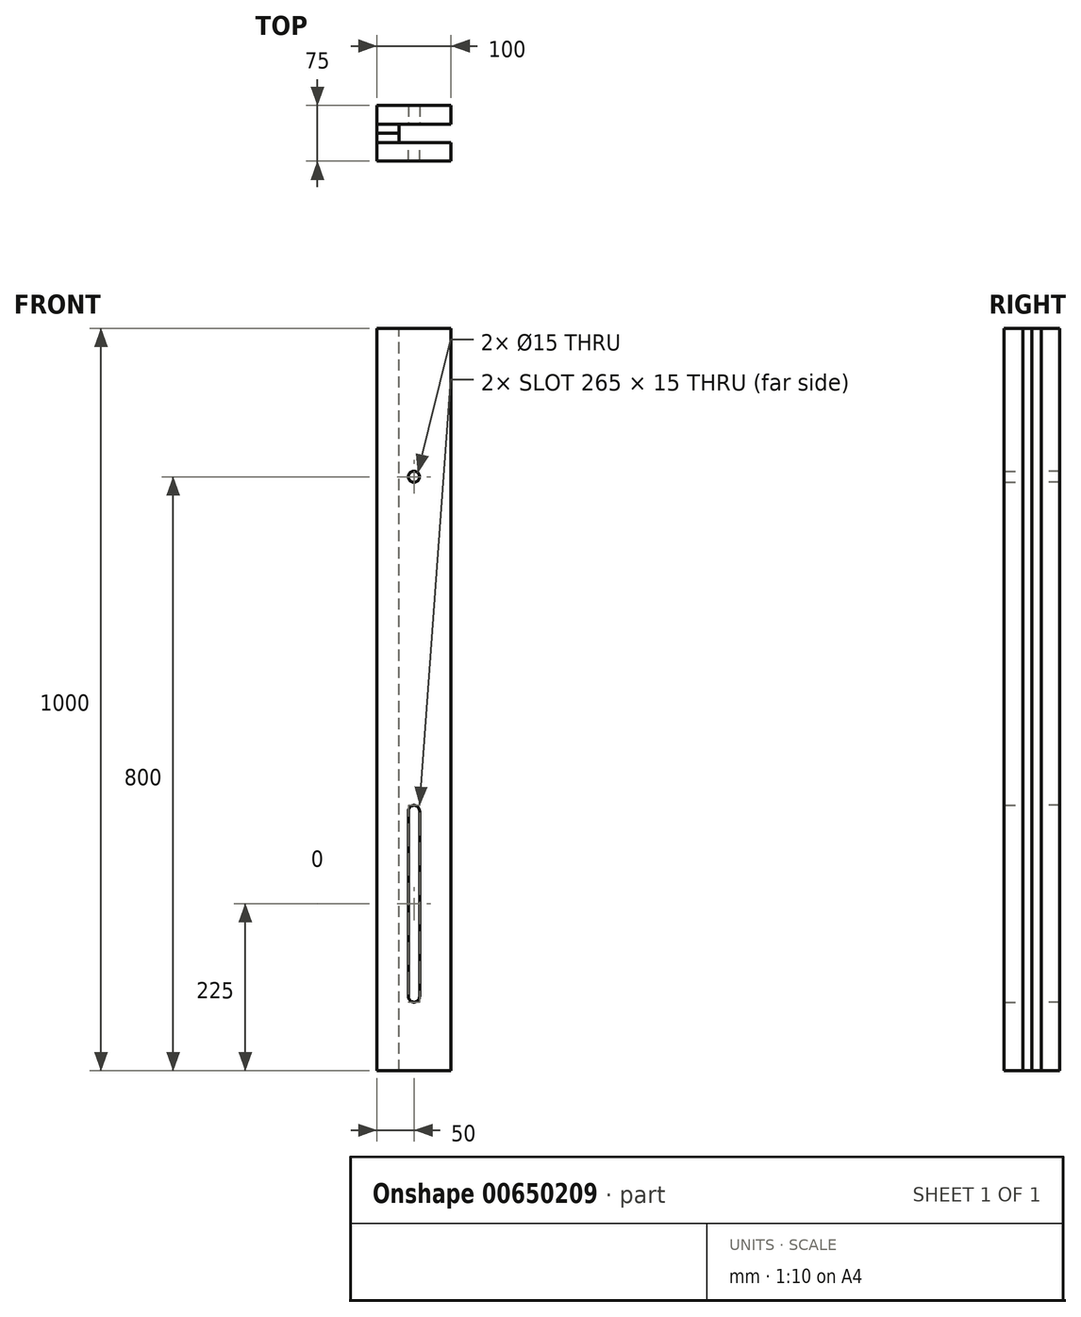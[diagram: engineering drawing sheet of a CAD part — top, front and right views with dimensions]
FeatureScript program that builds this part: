
annotation { "Feature Type Name" : "Feature", "Feature Type Description" : "" }
export const myFeature = defineFeature(function(context is Context, id is Id, definition is map)
    precondition{}
    {
        {
            var Q0;
            Q0=qCreatedBy(makeId("Front.planeOp"),FACE);
            var sketch = newSketch(context, id + "F0", { "sketchPlane" : qUnion([Q0])});
            skLineSegment(sketch, "E0.bottom", {"start": v(0, 0) * mm, "end": v(100, 0) * mm});
            skLineSegment(sketch, "E0.top", {"start": v(0, 1000) * mm, "end": v(100, 1000) * mm});
            skLineSegment(sketch, "E0.left", {"start": v(0, 0) * mm, "end": v(0, 1000) * mm});
            skLineSegment(sketch, "E0.right", {"start": v(100, 0) * mm, "end": v(100, 1000) * mm});
            skLineSegment(sketch, "E1", {"start": v(50, 100) * mm, "end": v(50, 350) * mm});
            skPoint(sketch, "E1.startSnap0", {"position": v(50, 0) * mm});
            skArc(sketch, "E2.0.startCap", {"start": v(57.5, 100) * mm, "mid": v(50, 92.5) * mm, "end": v(42.5, 100) * mm});
            skArc(sketch, "E2.0.endCap", {"start": v(42.5, 350) * mm, "mid": v(50, 357.5) * mm, "end": v(57.5, 350) * mm});
            skLineSegment(sketch, "E2.0.left", {"start": v(42.5, 100) * mm, "end": v(42.5, 350) * mm});
            skLineSegment(sketch, "E2.0.right", {"start": v(57.5, 100) * mm, "end": v(57.5, 350) * mm});
            skCircle(sketch, "E3", {"center": v(50, 800) * mm, "radius": 7.5 * mm});
            skPoint(sketch, "E3.centerSnap0", {"position": v(50, 1000) * mm});
            skSolve(sketch);
        }
        {
            var Q0;
            Q0=makeQuery(id+"F0.imprint","IMPRINT",FACE,{"disambiguationData":[TD([[makeQuery(id+"F0.imprint","IMPRINT",EDGE,{"derivedFrom":sQuery(id+"F0.wireOp",EDGE,"E0.bottom")}),1.0]])]});
            extrude(context, id + "F1", {"entities" : qUnion([Q0]), "depth" : 25 * mm, "offsetDistance" : 25 * mm});
        }
        {
            var Q0;
            Q0=makeQuery(id+"F1.opExtrude","SWEPT_FACE",FACE,{"disambiguationData":[OSD([sQuery(id+"F0.wireOp",EDGE,"E0.top")])]});
            var sketch = newSketch(context, id + "F2", { "sketchPlane" : qUnion([Q0])});
            skLineSegment(sketch, "E4.bottom", {"start": v(0, 0) * mm, "end": v(30, 0) * mm});
            skLineSegment(sketch, "E4.left", {"start": v(0, 0) * mm, "end": v(0, 12.5) * mm});
            skLineSegment(sketch, "E4.right", {"start": v(30, 0) * mm, "end": v(30, 12.5) * mm});
            skLineSegment(sketch, "E5", {"start": v(0, 12.5) * mm, "end": v(30, 12.5) * mm});
            skPoint(sketch, "E6.orphan", {"position": v(30, 25) * mm});
            skPoint(sketch, "E7.orphan", {"position": v(0, 25) * mm});
            skSolve(sketch);
        }
        {
            var Q0;
            {var subQ0=sQuery(id+"F2.wireOp",EDGE,"E4.bottom");Q0=makeQuery(id+"F2.imprint","IMPRINT",FACE,{"disambiguationData":[TD([[makeQuery(id+"F2.imprint","IMPRINT",EDGE,{"derivedFrom":subQ0}),1.0]])]});}
            var Q1;
            {var subQ0=sQuery(id+"F2.wireOp",EDGE,"E4.top");Q1=makeQuery(id+"F2.imprint","IMPRINT",FACE,{"disambiguationData":[TD([[makeQuery(id+"F2.imprint","IMPRINT",EDGE,{"derivedFrom":subQ0}),-1.0]])]});}
            var Q2;
            Q2=makeQuery(id+"F1.opExtrude","SWEPT_FACE",FACE,{"disambiguationData":[OSD([sQuery(id+"F0.wireOp",EDGE,"E0.bottom")])]});
            extrude(context, id + "F3", {"entities" : qUnion([Q0, Q1]), "endBound" : BoundingType.UP_TO_SURFACE, "oppositeDirection" : true, "depth" : 25 * mm, "endBoundEntityFace" : qUnion([Q2]), "offsetDistance" : 25 * mm});
        }
        {
            var Q0;
            Q0=makeQuery(id+"F1.opExtrude","SWEPT_BODY",BODY,{"disambiguationData":[OSD([sQuery(id+"F0.wireOp",EDGE,"E0.bottom"),sQuery(id+"F0.wireOp",EDGE,"E0.top"),sQuery(id+"F0.wireOp",EDGE,"E0.left"),sQuery(id+"F0.wireOp",EDGE,"E0.right"),sQuery(id+"F0.wireOp",EDGE,"118aecac-f219-4fef-92ac-b543d5344609.0.startCap"),sQuery(id+"F0.wireOp",EDGE,"118aecac-f219-4fef-92ac-b543d5344609.0.endCap"),sQuery(id+"F0.wireOp",EDGE,"118aecac-f219-4fef-92ac-b543d5344609.0.left"),sQuery(id+"F0.wireOp",EDGE,"118aecac-f219-4fef-92ac-b543d5344609.0.right"),sQuery(id+"F0.wireOp",EDGE,"E2.0.startCap"),sQuery(id+"F0.wireOp",EDGE,"E2.0.endCap"),sQuery(id+"F0.wireOp",EDGE,"E2.0.left"),sQuery(id+"F0.wireOp",EDGE,"E2.0.right")])]});
            var Q1;
            Q1=makeQuery(id+"F3.opExtrude","SWEPT_BODY",BODY,{"disambiguationData":[OSD([sQuery(id+"F2.wireOp",EDGE,"E4.bottom"),sQuery(id+"F2.wireOp",EDGE,"E4.left"),sQuery(id+"F2.wireOp",EDGE,"E4.right"),sQuery(id+"F2.wireOp",EDGE,"E5")])]});
            var Q2;
            Q2=makeQuery(id+"F3.opExtrude","SWEPT_FACE",FACE,{"disambiguationData":[OSD([sQuery(id+"F2.wireOp",EDGE,"E5")])]});
            mirror(context, id + "F4", {"entities" : qUnion([Q0, Q1]), "mirrorPlane" : qUnion([Q2])});
        }
    });
